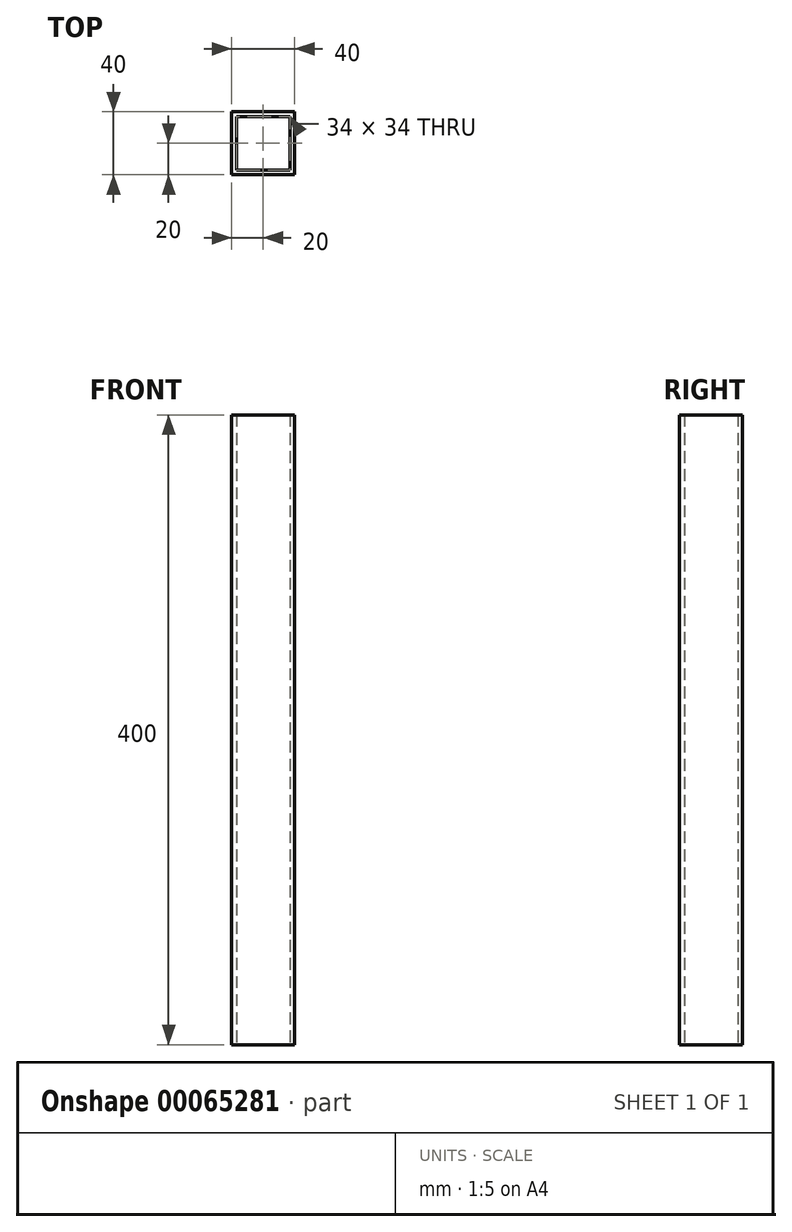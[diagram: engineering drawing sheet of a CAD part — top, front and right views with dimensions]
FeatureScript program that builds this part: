
annotation { "Feature Type Name" : "Feature", "Feature Type Description" : "" }
export const myFeature = defineFeature(function(context is Context, id is Id, definition is map)
    precondition{}
    {
        {
            var Q0;
            Q0=qCreatedBy(makeId("Top.planeOp"),FACE);
            var sketch = newSketch(context, id + "F0", { "sketchPlane" : qUnion([Q0])});
            skLineSegment(sketch, "E0.bottom", {"start": v(20, 20) * mm, "end": v(-20, 20) * mm});
            skLineSegment(sketch, "E0.top", {"start": v(20, -20) * mm, "end": v(-20, -20) * mm});
            skLineSegment(sketch, "E0.left", {"start": v(20, 20) * mm, "end": v(20, -20) * mm});
            skLineSegment(sketch, "E0.right", {"start": v(-20, 20) * mm, "end": v(-20, -20) * mm});
            skPoint(sketch, "E0.middle", {"position": v(0, 0) * mm});
            skLineSegment(sketch, "E1.0", {"start": v(17, 17) * mm, "end": v(-17, 17) * mm});
            skLineSegment(sketch, "E1.1", {"start": v(17, 17) * mm, "end": v(17, -17) * mm});
            skLineSegment(sketch, "E1.2", {"start": v(17, -17) * mm, "end": v(-17, -17) * mm});
            skLineSegment(sketch, "E1.3", {"start": v(-17, 17) * mm, "end": v(-17, -17) * mm});
            skSolve(sketch);
        }
        {
            var Q0;
            Q0 = qSketchRegion(id + "F0", true);
            extrude(context, id + "F1", {"entities" : qUnion([Q0]), "depth" : 400 * mm, "offsetDistance" : 25 * mm});
        }
    });
